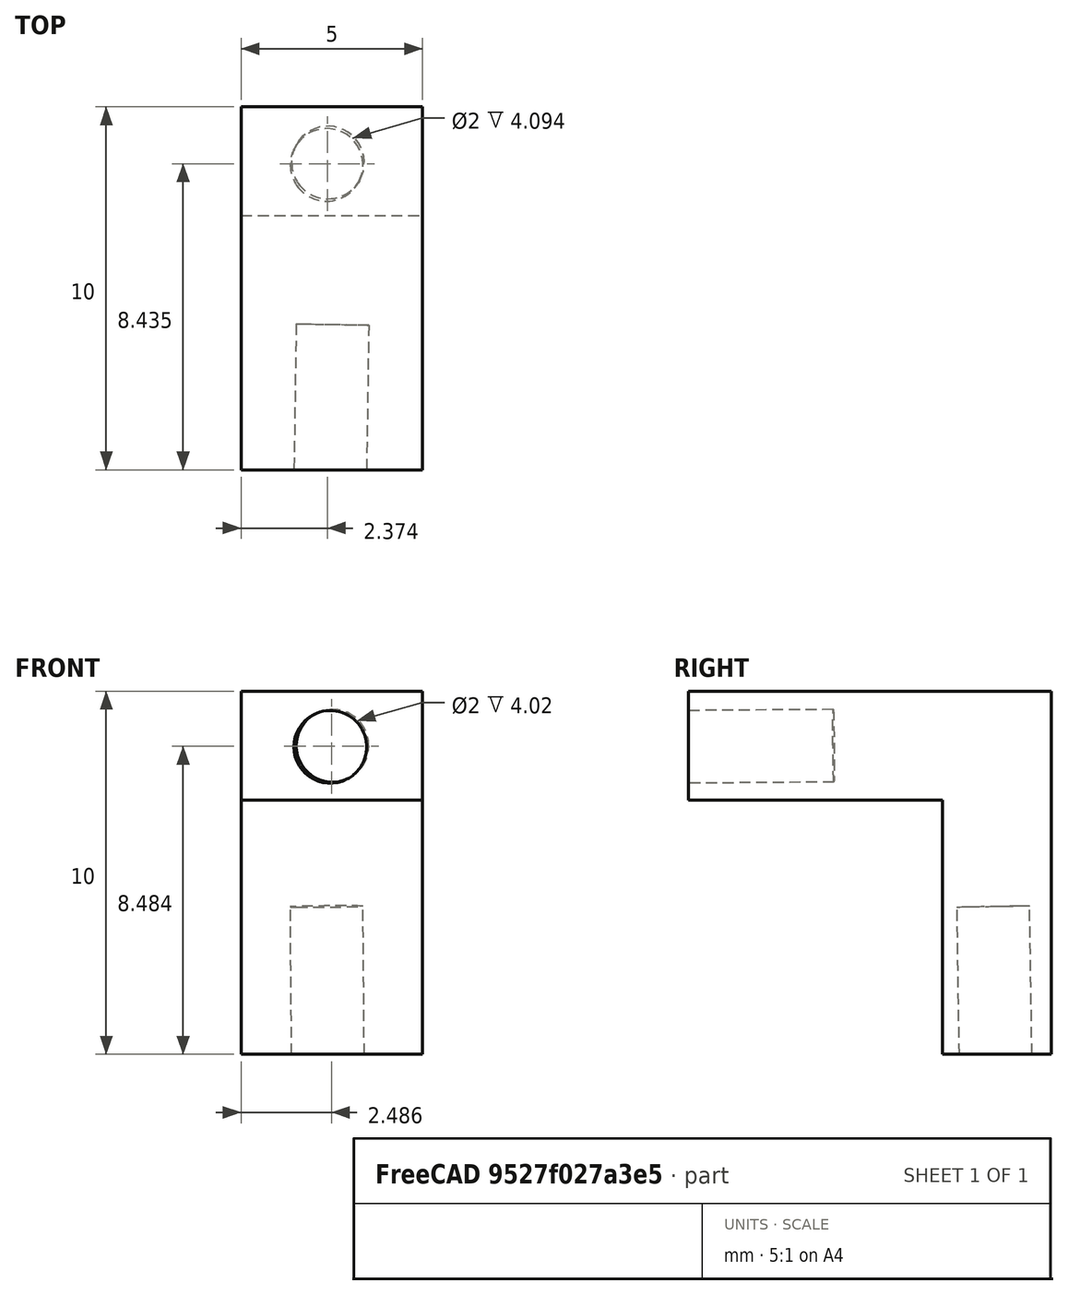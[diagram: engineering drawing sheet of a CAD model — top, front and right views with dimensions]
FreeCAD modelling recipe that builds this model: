
FCSTD DOCUMENT  (FreeCAD 0.16R6700 (Git))
Label: cad3
License: All rights reserved
LicenseURL: http://en.wikipedia.org/wiki/All_rights_reserved
objects: Part::FeaturePython×3, Part::Box×2, Part::Cylinder×2
note: 7 computed .brp shape members not serialized (recipe doc carries the construction recipe); baked Part::Feature solids carry a one-line shape summary decoded from their .brp

FEATURE [Part::Box] Box  label="Vertical Cube"
  Height = 10
  Length = 5
  Width = 3
FEATURE [Part::Box] Box001  label="Top Cube"
  Height = 3
  Length = 10
  Placement = pos=(5,-7,7) rot=(0,0,1;1.5708rad)
  Width = 5
FEATURE [Part::Cylinder] Cylinder  label="Screw Hole"
  Angle = 360
  Height = 5
  Placement = pos=(2.4,1.48138,-0.926) rot=(-0.006926,-0.006523,0.999955;3.74284rad)
  Radius = 1
FEATURE [Part::Cylinder] Cylinder001  label="Screw Hole 2"
  Angle = 360
  Height = 5
  Placement = pos=(2.51616,-2.9989,8.5) rot=(0.999625,0.010495,-0.025305;1.57924rad)
  Radius = 1
FEATURE [Part::FeaturePython] Cutout  # WARN: FeaturePython — macro-defined, semantics opaque (R4)
  Base = -> Box
  Mode = 3
  Tool = -> Cylinder
FEATURE [Part::FeaturePython] Cutout001  # WARN: FeaturePython — macro-defined, semantics opaque (R4)
  Base = -> Box001
  Mode = 3
  Tool = -> Cylinder001
FEATURE [Part::FeaturePython] Connect  # WARN: FeaturePython — macro-defined, semantics opaque (R4)
  Base = -> Cutout001
  Mode = 1
  Tool = -> Cutout
